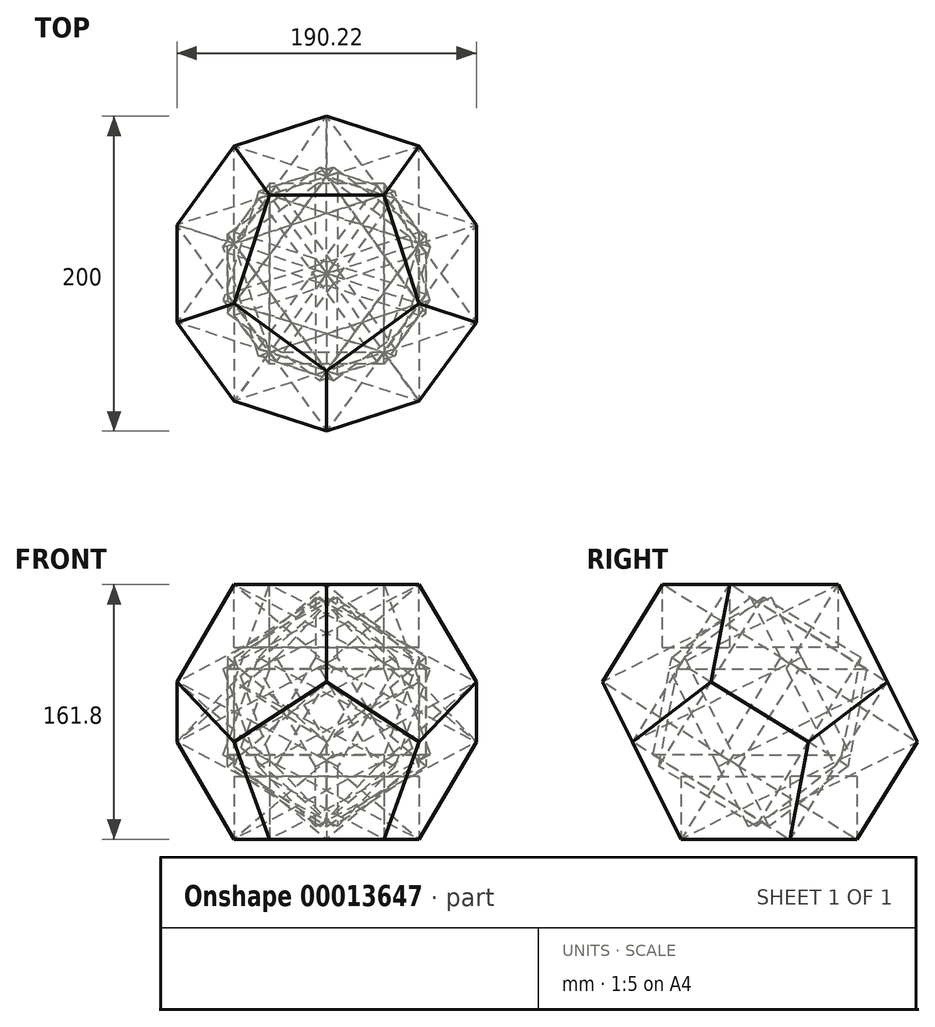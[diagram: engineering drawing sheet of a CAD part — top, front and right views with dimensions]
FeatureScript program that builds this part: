
annotation { "Feature Type Name" : "Feature", "Feature Type Description" : "" }
export const myFeature = defineFeature(function(context is Context, id is Id, definition is map)
    precondition{}
    {
        {
            var Q0;
            Q0=qCreatedBy(makeId("Top.planeOp"),FACE);
            var sketch = newSketch(context, id + "F0", { "sketchPlane" : qUnion([Q0])});
            skCircle(sketch, "E0.cCircle", {"center": v(0, 0) * mm, "radius": 50 * mm, "construction": true});
            skLineSegment(sketch, "E0.0", {"start": v(0, 61.8) * mm, "end": v(58.78, 19.1) * mm});
            skLineSegment(sketch, "E0.1", {"start": v(58.78, 19.1) * mm, "end": v(36.33, -50) * mm});
            skLineSegment(sketch, "E0.2", {"start": v(36.33, -50) * mm, "end": v(-36.33, -50) * mm});
            skLineSegment(sketch, "E0.3", {"start": v(-36.33, -50) * mm, "end": v(-58.78, 19.1) * mm});
            skLineSegment(sketch, "E0.4", {"start": v(-58.78, 19.1) * mm, "end": v(0, 61.8) * mm});
            skPoint(sketch, "E0.0.midPoint", {"position": v(29.39, 40.45) * mm});
            skSolve(sketch);
        }
        {
            var Q0;
            Q0=qCreatedBy(makeId("Right.planeOp"),FACE);
            var sketch = newSketch(context, id + "F1", { "sketchPlane" : qUnion([Q0])});
            skLineSegment(sketch, "E1", {"start": v(-50, 0) * mm, "end": v(-75.48, 50.96) * mm, "construction": true});
            skLineSegment(sketch, "E2", {"start": v(-50, 0) * mm, "end": v(0, 0) * mm, "construction": true});
            skLineSegment(sketch, "E3", {"start": v(0, 0) * mm, "end": v(0, 50.96) * mm, "construction": true});
            skSolve(sketch);
        }
        {
            var Q0;
            Q0=sQuery(id+"F0.wireOp",VERTEX,"E0.1.end");
            var Q1;
            Q1=sQuery(id+"F1.wireOp",VERTEX,"E1.start");
            var Q2;
            Q2=sQuery(id+"F1.wireOp",VERTEX,"E1.end");
            cPlane(context, id + "F2", {"entities" : qUnion([Q0, Q1, Q2]), "cplaneType" : CPlaneType.THREE_POINT, "offset" : 150 * mm, "width" : 150 * mm, "height" : 150 * mm});
        }
        {
            var Q0;
            Q0=qCreatedBy(id+"F2.planeOp",FACE);
            var sketch = newSketch(context, id + "F3", { "sketchPlane" : qUnion([Q0])});
            skCircle(sketch, "E4.cCircle", {"center": v(0, 72.36) * mm, "radius": 50 * mm, "construction": true});
            skLineSegment(sketch, "E4.0", {"start": v(36.33, 22.36) * mm, "end": v(-36.33, 22.36) * mm});
            skLineSegment(sketch, "E4.1", {"start": v(-36.33, 22.36) * mm, "end": v(-58.78, 91.46) * mm});
            skLineSegment(sketch, "E4.2", {"start": v(-58.78, 91.46) * mm, "end": v(0, 134.16) * mm});
            skLineSegment(sketch, "E4.3", {"start": v(0, 134.16) * mm, "end": v(58.78, 91.46) * mm});
            skLineSegment(sketch, "E4.4", {"start": v(58.78, 91.46) * mm, "end": v(36.33, 22.36) * mm});
            skPoint(sketch, "E4.0.midPoint", {"position": v(0, 22.36) * mm});
            skSolve(sketch);
        }
        {
            var Q0;
            Q0=qCreatedBy(makeId("Right.planeOp"),FACE);
            var sketch = newSketch(context, id + "F4", { "sketchPlane" : qUnion([Q0])});
            skLineSegment(sketch, "E5.0", {"start": v(-100, 100) * mm, "end": v(-80.9, 61.8) * mm, "construction": true});
            skLineSegment(sketch, "E6", {"start": v(-90.45, 80.9) * mm, "end": v(61.8, 80.9) * mm, "construction": true});
            skSolve(sketch);
        }
        {
            var Q0;
            Q0=makeQuery(id+"F0.imprint","IMPRINT",FACE,{"disambiguationData":[TD([[makeQuery(id+"F0.imprint","IMPRINT",EDGE,{"derivedFrom":sQuery(id+"F0.wireOp",EDGE,"E0.0")}),-1.0]])]});
            var Q1;
            Q1=qCreatedBy(id+"F2.planeOp",FACE);
            extrude(context, id + "F5", {"entities" : qUnion([Q0]), "endBoundEntity" : qUnion([Q1]), "depth" : 40 * mm});
        }
        {
            var Q0;
            Q0=makeQuery(id+"F3.imprint","IMPRINT",FACE,{"disambiguationData":[TD([[makeQuery(id+"F3.imprint","IMPRINT",EDGE,{"derivedFrom":sQuery(id+"F3.wireOp",EDGE,"E4.0")}),-1.0]])]});
            extrude(context, id + "F6", {"entities" : qUnion([Q0]), "oppositeDirection" : true, "depth" : 120 * mm});
        }
        {
            var Q0;
            Q0=makeQuery(id+"F6.opExtrude","SWEPT_BODY",BODY,{"disambiguationData":[OSD([sQuery(id+"F3.wireOp",EDGE,"E4.0"),sQuery(id+"F3.wireOp",EDGE,"E4.1"),sQuery(id+"F3.wireOp",EDGE,"E4.2"),sQuery(id+"F3.wireOp",EDGE,"E4.3"),sQuery(id+"F3.wireOp",EDGE,"E4.4")])]});
            var Q1;
            Q1=sQuery(id+"F1.wireOp",EDGE,"E3");
            circularPattern(context, id + "F7", {"entities" : qUnion([Q0]), "axis" : qUnion([Q1]), "angle" : 72 * degree, "instanceCount" : round(5)});
        }
        {
            var Q0;
            Q0=makeQuery(id+"F5.opExtrude","SWEPT_BODY",BODY,{"disambiguationData":[OSD([sQuery(id+"F0.wireOp",EDGE,"E0.0"),sQuery(id+"F0.wireOp",EDGE,"E0.1"),sQuery(id+"F0.wireOp",EDGE,"E0.2"),sQuery(id+"F0.wireOp",EDGE,"E0.3"),sQuery(id+"F0.wireOp",EDGE,"E0.4")])]});
            var Q1;
            Q1=makeQuery(id+"F6.opExtrude","SWEPT_BODY",BODY,{"disambiguationData":[OSD([sQuery(id+"F3.wireOp",EDGE,"E4.0"),sQuery(id+"F3.wireOp",EDGE,"E4.1"),sQuery(id+"F3.wireOp",EDGE,"E4.2"),sQuery(id+"F3.wireOp",EDGE,"E4.3"),sQuery(id+"F3.wireOp",EDGE,"E4.4")])]});
            var Q2;
            Q2=makeQuery(id+"F7.opPattern","COPY",BODY,{"derivedFrom":makeQuery(id+"F6.opExtrude","SWEPT_BODY",BODY,{"disambiguationData":[OSD([sQuery(id+"F3.wireOp",EDGE,"E4.0"),sQuery(id+"F3.wireOp",EDGE,"E4.1"),sQuery(id+"F3.wireOp",EDGE,"E4.2"),sQuery(id+"F3.wireOp",EDGE,"E4.3"),sQuery(id+"F3.wireOp",EDGE,"E4.4")])]}),"instanceName":"1"});
            var Q3;
            Q3=makeQuery(id+"F7.opPattern","COPY",BODY,{"derivedFrom":makeQuery(id+"F6.opExtrude","SWEPT_BODY",BODY,{"disambiguationData":[OSD([sQuery(id+"F3.wireOp",EDGE,"E4.0"),sQuery(id+"F3.wireOp",EDGE,"E4.1"),sQuery(id+"F3.wireOp",EDGE,"E4.2"),sQuery(id+"F3.wireOp",EDGE,"E4.3"),sQuery(id+"F3.wireOp",EDGE,"E4.4")])]}),"instanceName":"2"});
            var Q4;
            Q4=makeQuery(id+"F7.opPattern","COPY",BODY,{"derivedFrom":makeQuery(id+"F6.opExtrude","SWEPT_BODY",BODY,{"disambiguationData":[OSD([sQuery(id+"F3.wireOp",EDGE,"E4.0"),sQuery(id+"F3.wireOp",EDGE,"E4.1"),sQuery(id+"F3.wireOp",EDGE,"E4.2"),sQuery(id+"F3.wireOp",EDGE,"E4.3"),sQuery(id+"F3.wireOp",EDGE,"E4.4")])]}),"instanceName":"3"});
            var Q5;
            Q5=makeQuery(id+"F7.opPattern","COPY",BODY,{"derivedFrom":makeQuery(id+"F6.opExtrude","SWEPT_BODY",BODY,{"disambiguationData":[OSD([sQuery(id+"F3.wireOp",EDGE,"E4.0"),sQuery(id+"F3.wireOp",EDGE,"E4.1"),sQuery(id+"F3.wireOp",EDGE,"E4.2"),sQuery(id+"F3.wireOp",EDGE,"E4.3"),sQuery(id+"F3.wireOp",EDGE,"E4.4")])]}),"instanceName":"4"});
            var Q6;
            Q6=sQuery(id+"F4.wireOp",EDGE,"E6");
            transform(context, id + "F8", {"entities" : qUnion([Q0, Q1, Q2, Q3, Q4, Q5]), "transformType" : TransformType.ROTATION, "transformAxis" : qUnion([Q6]), "angle" : 180 * degree, "oppositeX" : false, "oppositeY" : false, "oppositeZ" : false, "makeCopy" : true});
        }
        {
            var Q0;
            Q0=makeQuery(id+"F8.opPattern","COPY",BODY,{"derivedFrom":makeQuery(id+"F7.opPattern","COPY",BODY,{"derivedFrom":makeQuery(id+"F6.opExtrude","SWEPT_BODY",BODY,{"disambiguationData":[OSD([sQuery(id+"F3.wireOp",EDGE,"E4.0"),sQuery(id+"F3.wireOp",EDGE,"E4.1"),sQuery(id+"F3.wireOp",EDGE,"E4.2"),sQuery(id+"F3.wireOp",EDGE,"E4.3"),sQuery(id+"F3.wireOp",EDGE,"E4.4")])]}),"instanceName":"2"}),"instanceName":"1"});
            var Q1;
            Q1=makeQuery(id+"F8.opPattern","COPY",BODY,{"derivedFrom":makeQuery(id+"F7.opPattern","COPY",BODY,{"derivedFrom":makeQuery(id+"F6.opExtrude","SWEPT_BODY",BODY,{"disambiguationData":[OSD([sQuery(id+"F3.wireOp",EDGE,"E4.0"),sQuery(id+"F3.wireOp",EDGE,"E4.1"),sQuery(id+"F3.wireOp",EDGE,"E4.2"),sQuery(id+"F3.wireOp",EDGE,"E4.3"),sQuery(id+"F3.wireOp",EDGE,"E4.4")])]}),"instanceName":"1"}),"instanceName":"1"});
            var Q2;
            Q2=makeQuery(id+"F8.opPattern","COPY",BODY,{"derivedFrom":makeQuery(id+"F6.opExtrude","SWEPT_BODY",BODY,{"disambiguationData":[OSD([sQuery(id+"F3.wireOp",EDGE,"E4.0"),sQuery(id+"F3.wireOp",EDGE,"E4.1"),sQuery(id+"F3.wireOp",EDGE,"E4.2"),sQuery(id+"F3.wireOp",EDGE,"E4.3"),sQuery(id+"F3.wireOp",EDGE,"E4.4")])]}),"instanceName":"1"});
            var Q3;
            Q3=makeQuery(id+"F8.opPattern","COPY",BODY,{"derivedFrom":makeQuery(id+"F7.opPattern","COPY",BODY,{"derivedFrom":makeQuery(id+"F6.opExtrude","SWEPT_BODY",BODY,{"disambiguationData":[OSD([sQuery(id+"F3.wireOp",EDGE,"E4.0"),sQuery(id+"F3.wireOp",EDGE,"E4.1"),sQuery(id+"F3.wireOp",EDGE,"E4.2"),sQuery(id+"F3.wireOp",EDGE,"E4.3"),sQuery(id+"F3.wireOp",EDGE,"E4.4")])]}),"instanceName":"4"}),"instanceName":"1"});
            var Q4;
            Q4=makeQuery(id+"F8.opPattern","COPY",BODY,{"derivedFrom":makeQuery(id+"F7.opPattern","COPY",BODY,{"derivedFrom":makeQuery(id+"F6.opExtrude","SWEPT_BODY",BODY,{"disambiguationData":[OSD([sQuery(id+"F3.wireOp",EDGE,"E4.0"),sQuery(id+"F3.wireOp",EDGE,"E4.1"),sQuery(id+"F3.wireOp",EDGE,"E4.2"),sQuery(id+"F3.wireOp",EDGE,"E4.3"),sQuery(id+"F3.wireOp",EDGE,"E4.4")])]}),"instanceName":"3"}),"instanceName":"1"});
            var Q5;
            Q5=makeQuery(id+"F8.opPattern","COPY",BODY,{"derivedFrom":makeQuery(id+"F5.opExtrude","SWEPT_BODY",BODY,{"disambiguationData":[OSD([sQuery(id+"F0.wireOp",EDGE,"E0.0"),sQuery(id+"F0.wireOp",EDGE,"E0.1"),sQuery(id+"F0.wireOp",EDGE,"E0.2"),sQuery(id+"F0.wireOp",EDGE,"E0.3"),sQuery(id+"F0.wireOp",EDGE,"E0.4")])]}),"instanceName":"1"});
            var Q6;
            Q6=sQuery(id+"F1.wireOp",EDGE,"E3");
            transform(context, id + "F9", {"entities" : qUnion([Q0, Q1, Q2, Q3, Q4, Q5]), "transformType" : TransformType.ROTATION, "transformAxis" : qUnion([Q6]), "angle" : 36 * degree, "oppositeX" : false, "oppositeY" : false, "oppositeZ" : false, "makeCopy" : false});
        }
    });
